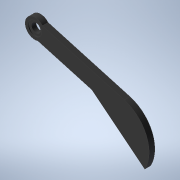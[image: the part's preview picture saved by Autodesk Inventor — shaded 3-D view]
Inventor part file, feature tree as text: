
AUTODESK INVENTOR PART (.ipt)
format: ipt  version: 2020.2 (Build 242310000, 310)  size: 176,128 bytes
history: native  units: mm
features: other x3, sketch x3, extrude x3, hole x1
ambient origin geometry x8: Origin, YZ Plane, XZ Plane, XY Plane, X Axis, Y Axis, Z Axis, Center Point
bodies: Body1 (feature_tree)
feature tree (10):
  other  "ソリッド1"
  sketch  "スケッチ1"
  extrude  "押し出し1"  Depth=5.0mm TaperAngle=0.0deg
  hole  "穴1"  [1 undecoded]
  extrude  "押し出し2"  Depth=5.0mm TaperAngle=0.0deg
  extrude  "押し出し3"  Depth=12.0mm
  sketch  "スケッチ2"
  sketch  "スケッチ3"
  other  "断面エッジを投影1"
  other  "断面エッジを投影2"
note: 1 required parameter value undecoded (feature->parameter linkage not recoverable at this tier; creation-order binding heuristic only, values carry confidence <= 0.55)
